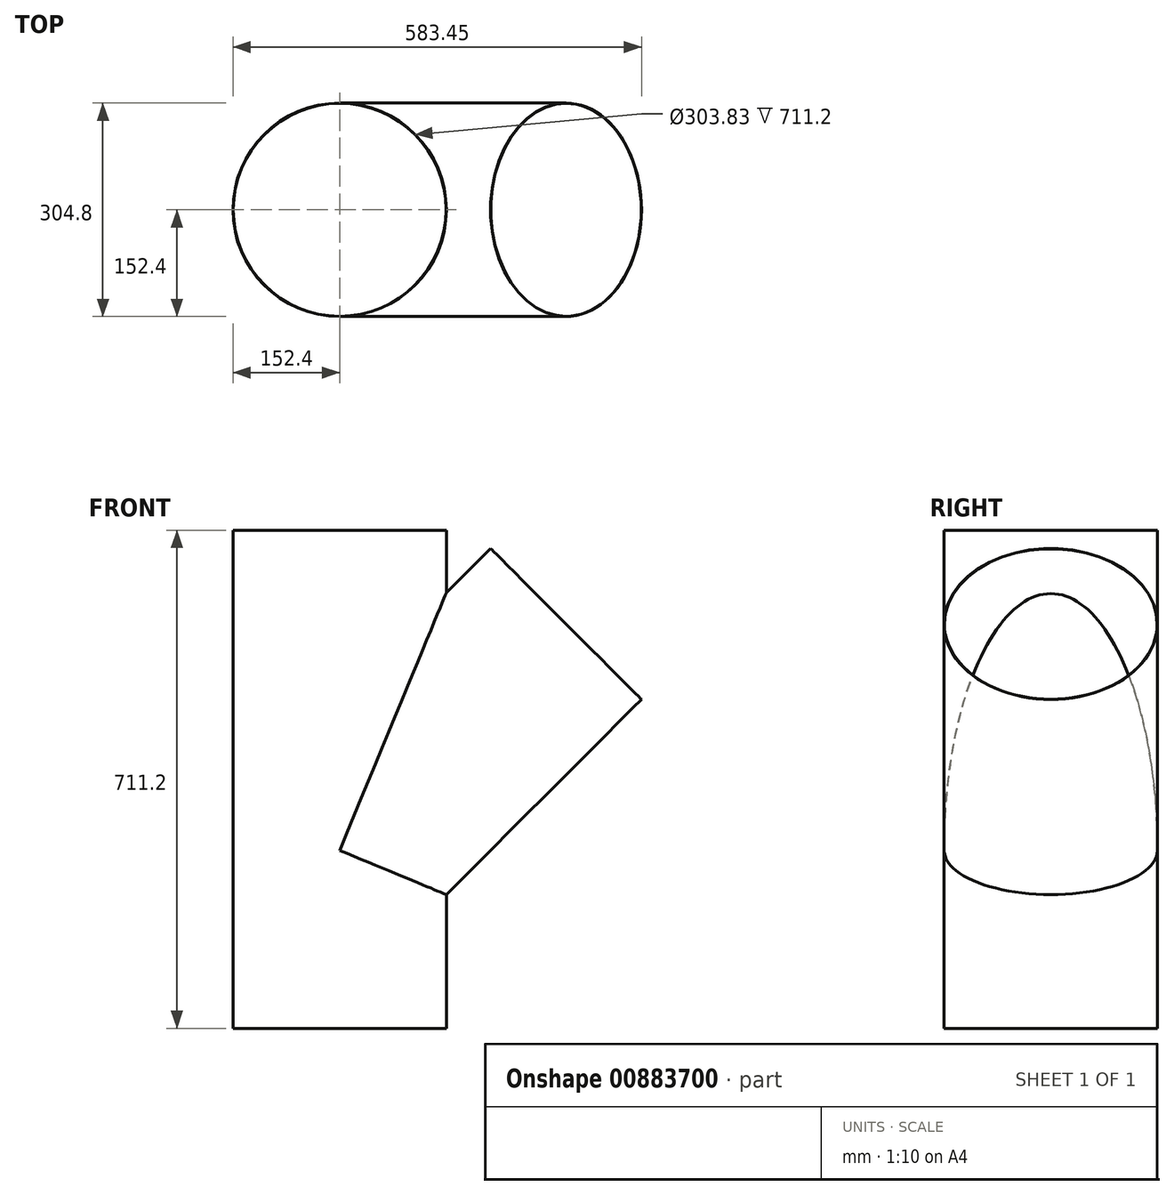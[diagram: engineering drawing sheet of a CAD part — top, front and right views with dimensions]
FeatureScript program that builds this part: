
annotation { "Feature Type Name" : "Feature", "Feature Type Description" : "" }
export const myFeature = defineFeature(function(context is Context, id is Id, definition is map)
    precondition{}
    {
        {
            var Q0;
            Q0=qCreatedBy(makeId("Front.planeOp"),FACE);
            var sketch = newSketch(context, id + "F0", { "sketchPlane" : qUnion([Q0])});
            skLineSegment(sketch, "E0", {"start": v(0, 0) * mm, "end": v(0, 711.2) * mm});
            skLineSegment(sketch, "E1", {"start": v(0, 254) * mm, "end": v(323.29, 577.29) * mm});
            skSolve(sketch);
        }
        {
            var Q0;
            Q0=sQuery(id+"F0.wireOp",VERTEX,"E0.start");
            var Q1;
            Q1=sQuery(id+"F0.wireOp",EDGE,"E0");
            cPlane(context, id + "F1", {"entities" : qUnion([Q0, Q1]), "cplaneType" : CPlaneType.LINE_POINT, "offset" : 25.4 * mm, "width" : 152.4 * mm, "height" : 152.4 * mm});
        }
        {
            var Q0;
            Q0=qCreatedBy(id+"F1.planeOp",FACE);
            var sketch = newSketch(context, id + "F2", { "sketchPlane" : qUnion([Q0])});
            skCircle(sketch, "E2", {"center": v(0, 0) * mm, "radius": 152.4 * mm});
            skCircle(sketch, "E3", {"center": v(0, 0) * mm, "radius": 151.92 * mm});
            skSolve(sketch);
        }
        {
            var Q0;
            Q0=makeQuery(id+"F2.imprint","IMPRINT",FACE,{"disambiguationData":[TD([[makeQuery(id+"F2.imprint","IMPRINT",EDGE,{"derivedFrom":sQuery(id+"F2.wireOp",EDGE,"E2")}),1.0]])]});
            var Q1;
            Q1=sQuery(id+"F2.wireOp",EDGE,"E2");
            var Q2;
            Q2=sQuery(id+"F0.wireOp",EDGE,"E0");
            sweep(context, id + "F3", {"profiles" : qUnion([Q0]), "surfaceProfiles" : qUnion([Q1]), "path" : qUnion([Q2])});
        }
        {
            var Q0;
            Q0=sQuery(id+"F0.wireOp",VERTEX,"E1.end");
            var Q1;
            Q1=sQuery(id+"F0.wireOp",EDGE,"E1");
            cPlane(context, id + "F4", {"entities" : qUnion([Q0, Q1]), "cplaneType" : CPlaneType.LINE_POINT, "offset" : 25.4 * mm, "width" : 152.4 * mm, "height" : 152.4 * mm});
        }
        {
            var Q0;
            Q0=qCreatedBy(id+"F4.planeOp",FACE);
            var sketch = newSketch(context, id + "F5", { "sketchPlane" : qUnion([Q0])});
            skPoint(sketch, "E4.0", {"position": v(0, 179.6) * mm});
            skCircle(sketch, "E5", {"center": v(0, 179.6) * mm, "radius": 152.4 * mm});
            skCircle(sketch, "E6", {"center": v(0, 179.6) * mm, "radius": 151.92 * mm});
            skSolve(sketch);
        }
        {
            var Q0;
            Q0=makeQuery(id+"F5.imprint","IMPRINT",FACE,{"disambiguationData":[TD([[makeQuery(id+"F5.imprint","IMPRINT",EDGE,{"derivedFrom":sQuery(id+"F5.wireOp",EDGE,"E5")}),1.0]])]});
            var Q1;
            Q1=sQuery(id+"F5.wireOp",EDGE,"E5");
            var Q2;
            Q2=sQuery(id+"F0.wireOp",EDGE,"E1");
            sweep(context, id + "F6", {"operationType" : NewBodyOperationType.ADD, "profiles" : qUnion([Q0]), "surfaceProfiles" : qUnion([Q1]), "path" : qUnion([Q2])});
        }
        {
            var Q0;
            Q0=makeQuery(id+"F2.imprint","IMPRINT",FACE,{"disambiguationData":[TD([[makeQuery(id+"F2.imprint","IMPRINT",EDGE,{"derivedFrom":sQuery(id+"F2.wireOp",EDGE,"E3")}),1.0]])]});
            extrude(context, id + "F7", {"entities" : qUnion([Q0]), "operationType" : NewBodyOperationType.REMOVE, "endBound" : BoundingType.THROUGH_ALL, "depth" : 762 * mm, "offsetDistance" : 25.4 * mm});
        }
        {
            var Q0;
            Q0=makeQuery(id+"F5.imprint","IMPRINT",FACE,{"disambiguationData":[TD([[makeQuery(id+"F5.imprint","IMPRINT",EDGE,{"derivedFrom":sQuery(id+"F5.wireOp",EDGE,"E6")}),1.0]])]});
            extrude(context, id + "F8", {"entities" : qUnion([Q0]), "operationType" : NewBodyOperationType.REMOVE, "oppositeDirection" : true, "depth" : 457.2 * mm, "offsetDistance" : 25.4 * mm});
        }
    });
